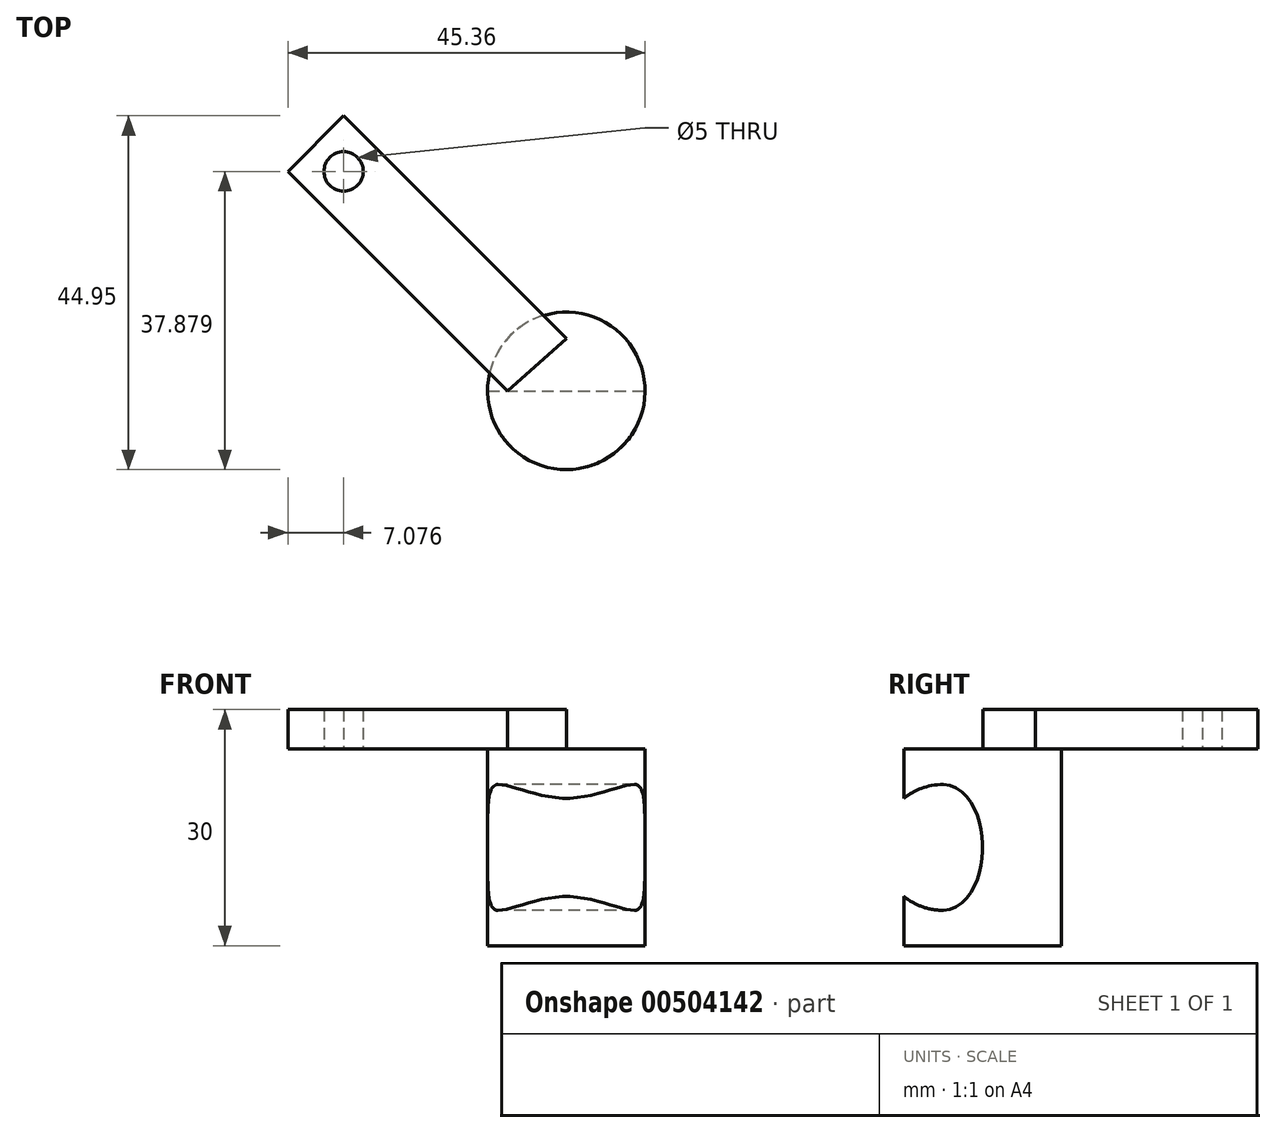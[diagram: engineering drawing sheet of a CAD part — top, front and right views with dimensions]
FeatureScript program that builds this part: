
annotation { "Feature Type Name" : "Feature", "Feature Type Description" : "" }
export const myFeature = defineFeature(function(context is Context, id is Id, definition is map)
    precondition{}
    {
        {
            var Q0;
            Q0=qCreatedBy(makeId("Top.planeOp"),FACE);
            var sketch = newSketch(context, id + "F0", { "sketchPlane" : qUnion([Q0])});
            skCircle(sketch, "E0", {"center": v(0, 0) * mm, "radius": 10 * mm});
            skSolve(sketch);
        }
        {
            var Q0;
            Q0 = qSketchRegion(id + "F0", true);
            extrude(context, id + "F1", {"entities" : qUnion([Q0]), "depth" : 25 * mm, "offsetDistance" : 25 * mm});
        }
        {
            var Q0;
            Q0=qCreatedBy(makeId("Right.planeOp"),FACE);
            var sketch = newSketch(context, id + "F2", { "sketchPlane" : qUnion([Q0])});
            skEllipse(sketch, "E1", {"center": v(-5, 12.5) * mm, "majorRadius": 8 * mm, "minorRadius": 5 * mm, "majorAxis": v(0, 1)});
            skArc(sketch, "E2", {"start": v(-5, 20.5) * mm, "mid": v(-13, 12.5) * mm, "end": v(-5, 4.5) * mm});
            skSolve(sketch);
        }
        {
            var Q0;
            Q0 = qSketchRegion(id + "F2", true);
            extrude(context, id + "F3", {"entities" : qUnion([Q0]), "operationType" : NewBodyOperationType.REMOVE, "endBound" : BoundingType.SYMMETRIC, "depth" : 25 * mm, "offsetDistance" : 25 * mm});
        }
        {
            var Q0;
            Q0=makeQuery(id+"F1.opExtrude","CAP_FACE",FACE,{"disambiguationData":[OSD([sQuery(id+"F0.wireOp",EDGE,"E0")])],"isStart":false});
            var sketch = newSketch(context, id + "F4", { "sketchPlane" : qUnion([Q0])});
            skSolve(sketch);
        }
        {
            var Q0;
            Q0=makeQuery(id+"F4.imprint","IMPRINT",FACE,{"disambiguationData":[TD([[makeQuery(id+"F4.imprint","IMPRINT",EDGE,{"derivedFrom":makeQuery(id+"F1.opExtrude","CAP_EDGE",EDGE,{"disambiguationData":[OSD([sQuery(id+"F0.wireOp",EDGE,"E0")])],"isStart":false})}),1.0]])]});
            var sketch = newSketch(context, id + "F5", { "sketchPlane" : qUnion([Q0])});
            skLineSegment(sketch, "E3", {"start": v(0, 6.67) * mm, "end": v(-28.28, 34.95) * mm});
            skLineSegment(sketch, "E4", {"start": v(-28.28, 34.95) * mm, "end": v(-35.36, 27.88) * mm});
            skLineSegment(sketch, "E5", {"start": v(-35.36, 27.88) * mm, "end": v(-7.48, 0) * mm});
            skLineSegment(sketch, "E6", {"start": v(-7.48, 0) * mm, "end": v(0, 6.67) * mm});
            skCircle(sketch, "E7", {"center": v(-28.28, 27.88) * mm, "radius": 2.5 * mm});
            skSolve(sketch);
        }
        {
            var Q0;
            Q0 = qSketchRegion(id + "F5", true);
            extrude(context, id + "F6", {"entities" : qUnion([Q0]), "operationType" : NewBodyOperationType.ADD, "depth" : 5 * mm, "offsetDistance" : 25 * mm});
        }
    });
